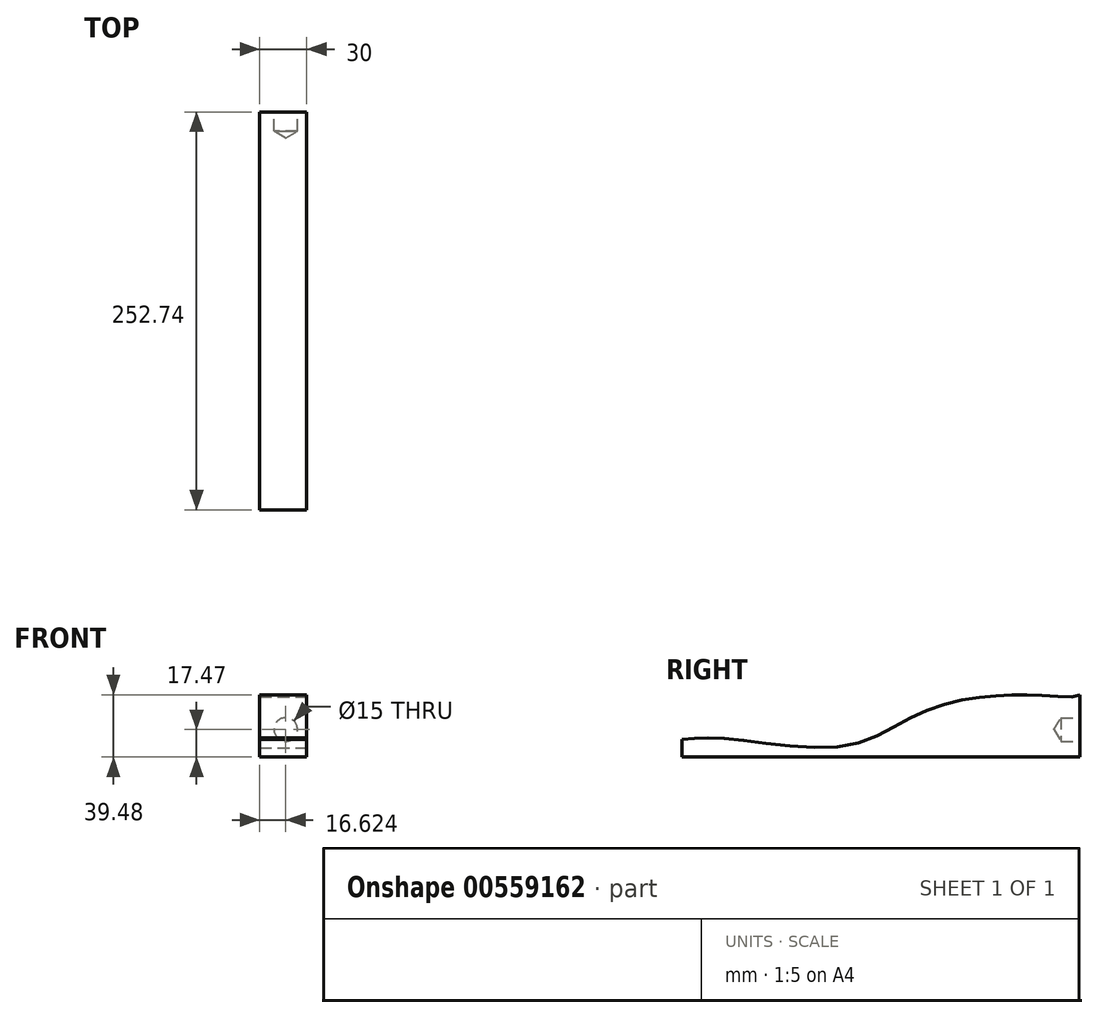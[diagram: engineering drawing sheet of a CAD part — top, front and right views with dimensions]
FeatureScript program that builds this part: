
annotation { "Feature Type Name" : "Feature", "Feature Type Description" : "" }
export const myFeature = defineFeature(function(context is Context, id is Id, definition is map)
    precondition{}
    {
        {
            var Q0;
            Q0=qCreatedBy(makeId("Right.planeOp"),FACE);
            var sketch = newSketch(context, id + "F0", { "sketchPlane" : qUnion([Q0])});
            skLineSegment(sketch, "E0", {"start": v(-131.75, 0) * mm, "end": v(-131.75, -17.47) * mm});
            skLineSegment(sketch, "E1", {"start": v(-131.75, -17.47) * mm, "end": v(120.99, -17.47) * mm});
            skLineSegment(sketch, "E2", {"start": v(120.99, -18.29) * mm, "end": v(120.99, 49.73) * mm});
            skLineSegment(sketch, "E3", {"start": v(120.99, 49.73) * mm, "end": v(-131.75, 8.04) * mm});
            skLineSegment(sketch, "E4", {"start": v(-131.75, 8.04) * mm, "end": v(-131.75, 0) * mm});
            skFitSpline(sketch, "E5", {"points": [v(-131.75, -6.34) * mm, v(-102.23, -5.78) * mm, v(-27.21, -10.26) * mm, v(20.93, 11.01) * mm, v(65.35, 21.27) * mm, v(99.3, 21.46) * mm, v(120.99, 21.83) * mm, v(120.99, 24.63) * mm, v(120.99, 32.28) * mm, v(120.99, 49.73) * mm, v(119.49, 49.48) * mm, v(-7.58, 28.52) * mm, v(-104.26, 12.58) * mm, v(-131.75, 8.04) * mm], "startDerivative": vector(346.59, 34.76) * mm, "endDerivative": vector(-347.6, -56.31) * mm});
            skSolve(sketch);
        }
        {
            var Q0;
            Q0=makeQuery(id+"F0.imprint","IMPRINT",FACE,{"disambiguationData":[TD([[makeQuery(id+"F0.imprint","IMPRINT",EDGE,{"derivedFrom":sQuery(id+"F0.wireOp",EDGE,"E0")}),1.0]])]});
            extrude(context, id + "F1", {"entities" : qUnion([Q0]), "depth" : 30 * mm, "offsetDistance" : 25.4 * mm});
        }
        {
            var Q0;
            Q0=makeQuery(id+"F1.opExtrude","SWEPT_FACE",FACE,{"disambiguationData":[OSD([sQuery(id+"F0.wireOp",EDGE,"E2")])]});
            var sketch = newSketch(context, id + "F2", { "sketchPlane" : qUnion([Q0])});
            skCircle(sketch, "E6", {"center": v(-15.83, 14.95) * mm, "radius": 6.9 * mm});
            skCircle(sketch, "E7", {"center": v(-16.62, 0) * mm, "radius": 7.04 * mm});
            skSolve(sketch);
        }
        {
            var Q0;
            Q0=sQuery(id+"F2.wireOp",VERTEX,"E7.center");
            var Q1;
            Q1=makeQuery(id+"F1.opExtrude","SWEPT_BODY",BODY,{"disambiguationData":[OSD([sQuery(id+"F0.wireOp",EDGE,"E0"),sQuery(id+"F0.wireOp",EDGE,"E1"),sQuery(id+"F0.wireOp",EDGE,"E2"),sQuery(id+"F0.wireOp",EDGE,"E5")])]});
            hole(context, id + "F3", {"style" : HoleStyle.SIMPLE, "endStyle" : HoleEndStyle.BLIND, "holeDiameter" : 15 * mm, "holeDepth" : 12 * mm, "isTappedThrough" : true, "tappedDepth" : 12 * mm, "tapClearance" : 3, "locations" : qUnion([Q0]), "scope" : qUnion([Q1])});
        }
    });
